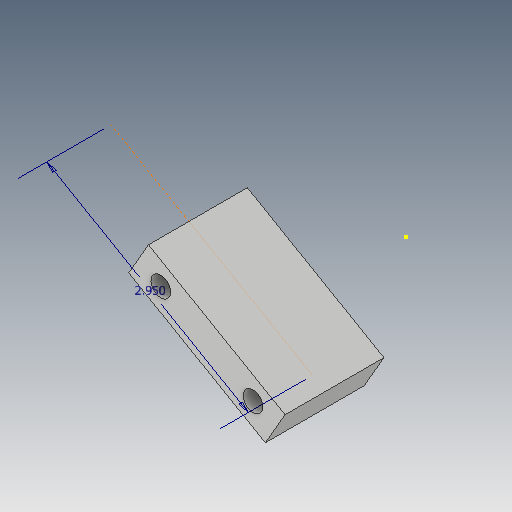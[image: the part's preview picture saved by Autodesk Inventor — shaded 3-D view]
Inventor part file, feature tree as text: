
AUTODESK INVENTOR PART (.ipt)
format: ipt  version: 2019.4 (Build 234330000, 330)  size: 114,176 bytes
history: native  units: in
note: dims shown in document units (in); Inventor stores cm internally (conversion verified against a paired STEP export)
features: sketch x2
ambient origin geometry x8: Origin, YZ Plane, XZ Plane, XY Plane, X Axis, Y Axis, Z Axis, Center Point
bodies: Solid1 (feature_tree), Solid2 (feature_tree)
feature tree (2):
  sketch  "Sketch1"  dims[d0=2.95in]
  sketch  "Sketch2"
